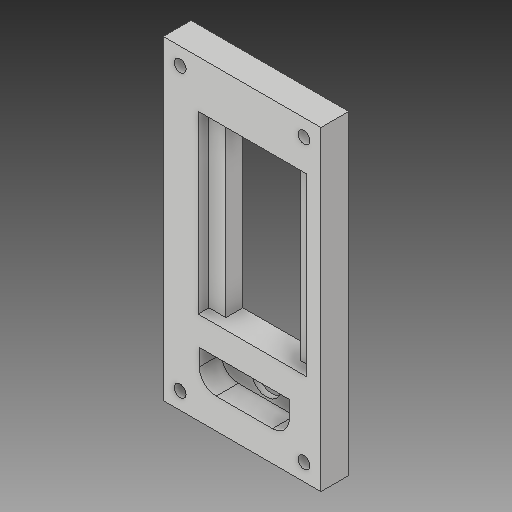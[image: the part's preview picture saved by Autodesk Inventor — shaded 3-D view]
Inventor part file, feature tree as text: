
AUTODESK INVENTOR PART (.ipt)
format: ipt  version: 2018 (Build 220112000, 112)  size: 176,640 bytes
history: native  units: in
note: dims shown in document units (in); Inventor stores cm internally (conversion verified against a paired STEP export)
features: sketch x4, extrude x4, plane x4, hole x4, fillet x1, projected_geometry x1
ambient origin geometry x8: Origin, YZ Plane, XZ Plane, XY Plane, X Axis, Y Axis, Z Axis, Center Point
bodies: Solid1 (feature_tree)
feature tree (18):
  sketch  "Sketch1"  dims[d0=3.5in d1=7.0in]
  extrude  "Extrusion1"  Depth=7.0in
  plane  "Work Plane1"
  plane  "Work Plane2"
  plane  "Work Plane3"
  plane  "Work Plane4"
  hole  "Hole2"  [1 undecoded]
  extrude  "Extrusion2"  Depth=1.65in
  sketch  "Sketch3"  dims[d4=1.65in d6=1.0496in]
  extrude  "Extrusion3"  Depth=3.9in
  extrude  "Extrusion4"  Depth=2.4in
  fillet  "Fillet1"  Radius=0.252in
  hole  "Hole5"  [1 undecoded]
  sketch  "Sketch2"  dims[d2=2.45in d3=3.9in]
  hole  "Hole1"  [1 undecoded]
  projected_geometry  "Projected Loop1"
  sketch  "Sketch5"  dims[d7=0.125in d8=0.0in d9=0.6562in d10=0.75in d11=0.375in d12=0.25in d13=0.5635in d14=1.0in d15=0.0in d16=3.9in d17=2.4in d18=0.252in d19=0.0in d20=1.0in d21=1.0in d22=0.75in d23=0.493in d24=0.0in d26=0.125in d27=0.493in d28=0.0in d29=0.024in d30=0.7126in d31=0.375in d39=0.266in d40=0.75in d41=0.375in d42=0.25in d43=0.5635in d44=1.0in d45=0.0in]
  hole  "Hole4"  [1 undecoded]
note: 4 required parameter values undecoded (feature->parameter linkage not recoverable at this tier; creation-order binding heuristic only, values carry confidence <= 0.55)
